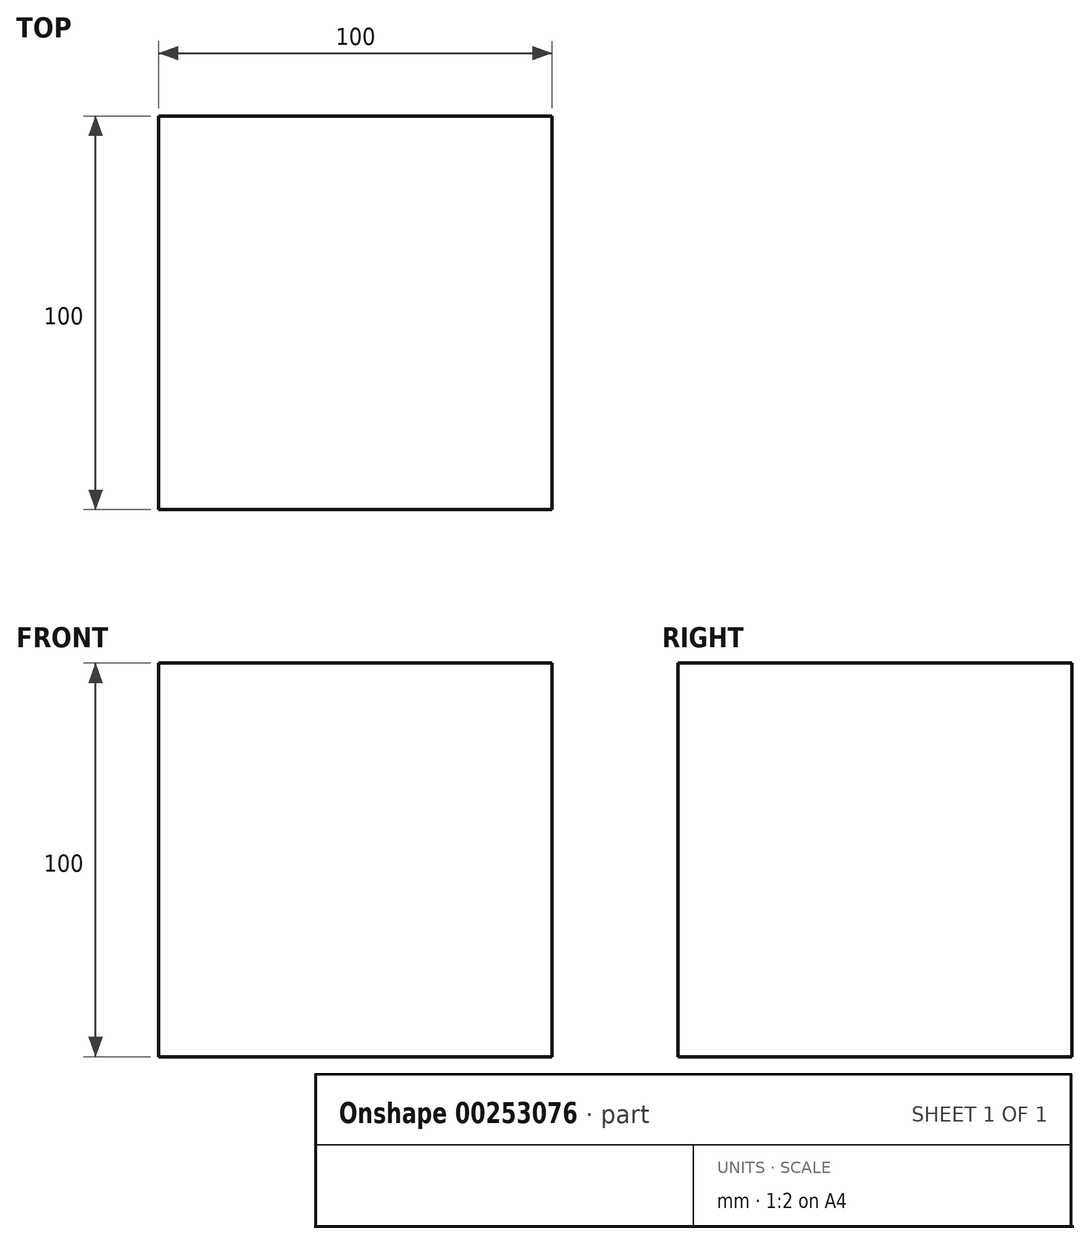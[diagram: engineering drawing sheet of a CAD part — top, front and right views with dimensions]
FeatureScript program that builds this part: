
annotation { "Feature Type Name" : "Feature", "Feature Type Description" : "" }
export const myFeature = defineFeature(function(context is Context, id is Id, definition is map)
    precondition{}
    {
        {
            var Q0;
            Q0=qCreatedBy(makeId("Front.planeOp"),FACE);
            var sketch = newSketch(context, id + "F0", { "sketchPlane" : qUnion([Q0])});
            skLineSegment(sketch, "E0", {"start": v(0, 0) * mm, "end": v(0, 35) * mm});
            skLineSegment(sketch, "E1", {"start": v(0, 35) * mm, "end": v(65, 35) * mm});
            skLineSegment(sketch, "E2", {"start": v(65, 35) * mm, "end": v(65, 100) * mm});
            skLineSegment(sketch, "E3", {"start": v(65, 100) * mm, "end": v(100, 100) * mm});
            skLineSegment(sketch, "E4", {"start": v(100, 100) * mm, "end": v(100, 0) * mm});
            skLineSegment(sketch, "E5", {"start": v(100, 0) * mm, "end": v(0, 0) * mm});
            skSolve(sketch);
        }
        {
            var Q0;
            Q0=makeQuery(id+"F0.imprint","IMPRINT",FACE,{"disambiguationData":[TD([[makeQuery(id+"F0.imprint","IMPRINT",EDGE,{"derivedFrom":sQuery(id+"F0.wireOp",EDGE,"E0")}),-1.0]])]});
            extrude(context, id + "F1", {"entities" : qUnion([Q0]), "depth" : 100 * mm});
        }
        {
            var Q0;
            Q0=makeQuery(id+"F1.opExtrude","SWEPT_FACE",FACE,{"disambiguationData":[OSD([sQuery(id+"F0.wireOp",EDGE,"E1")])]});
            var sketch = newSketch(context, id + "F2", { "sketchPlane" : qUnion([Q0])});
            skLineSegment(sketch, "E6", {"start": v(65, 0) * mm, "end": v(0, 0) * mm});
            skLineSegment(sketch, "E7", {"start": v(0, 0) * mm, "end": v(0, -100) * mm});
            skLineSegment(sketch, "E8", {"start": v(0, -100) * mm, "end": v(65, -100) * mm});
            skLineSegment(sketch, "E9", {"start": v(65, -100) * mm, "end": v(65, 0) * mm});
            skSolve(sketch);
        }
        {
            var Q0;
            Q0 = qSketchRegion(id + "F2", true);
            extrude(context, id + "F3", {"entities" : qUnion([Q0]), "operationType" : NewBodyOperationType.ADD, "depth" : 65 * mm});
        }
    });
